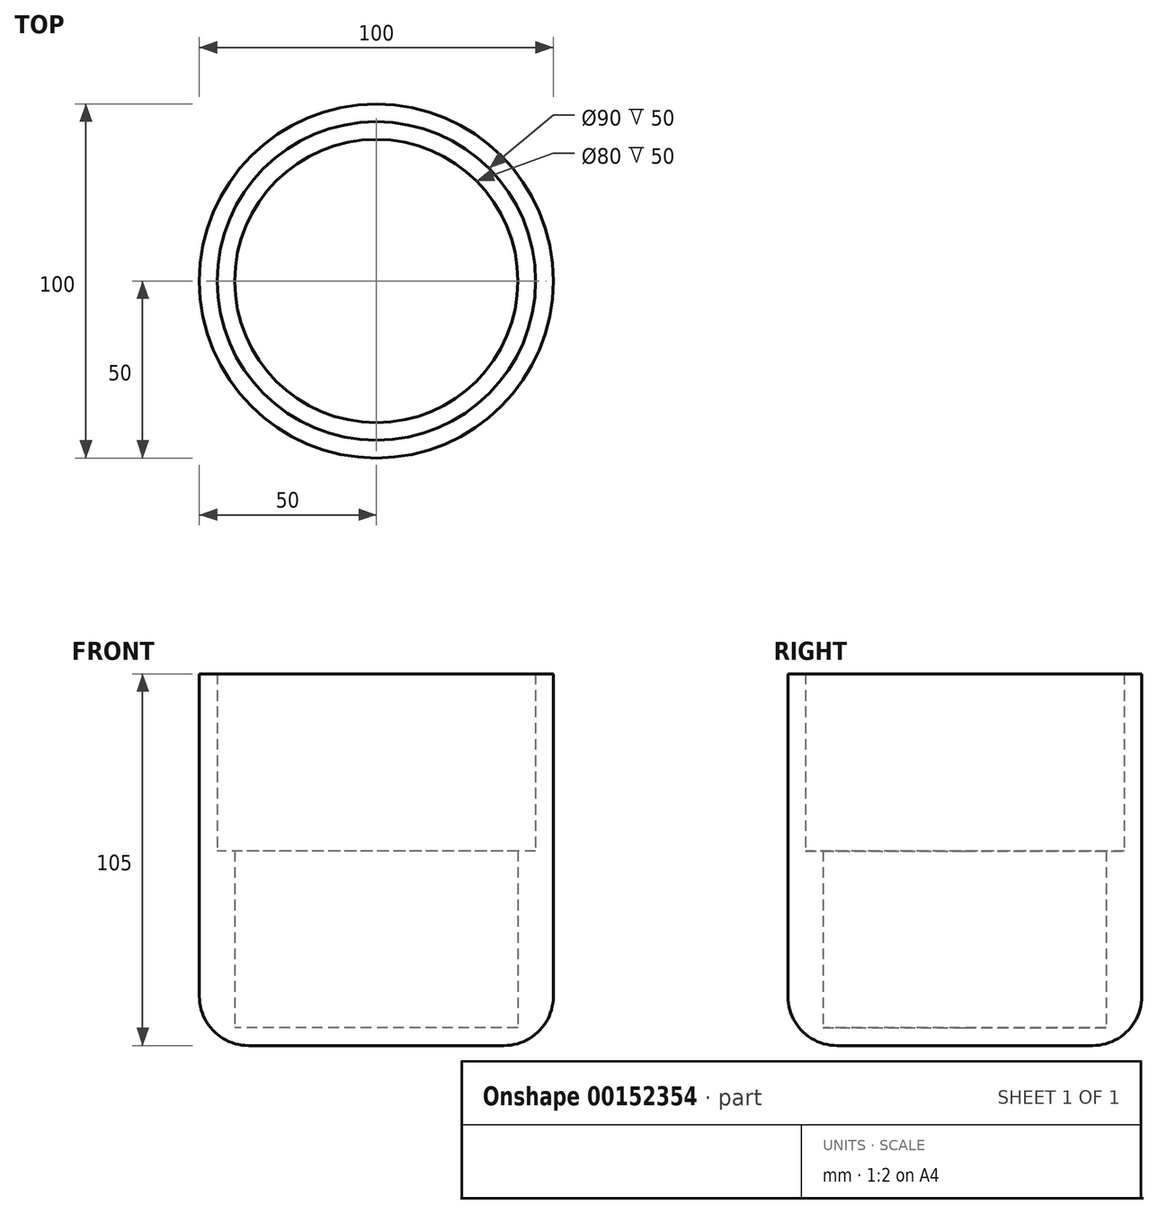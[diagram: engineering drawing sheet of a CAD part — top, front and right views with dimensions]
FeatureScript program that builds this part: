
annotation { "Feature Type Name" : "Feature", "Feature Type Description" : "" }
export const myFeature = defineFeature(function(context is Context, id is Id, definition is map)
    precondition{}
    {
        {
            var Q0;
            Q0=qCreatedBy(makeId("Top.planeOp"),FACE);
            var sketch = newSketch(context, id + "F0", { "sketchPlane" : qUnion([Q0])});
            skCircle(sketch, "E0", {"center": v(0, 0) * mm, "radius": 50 * mm});
            skCircle(sketch, "E1", {"center": v(0, 0) * mm, "radius": 45 * mm});
            skCircle(sketch, "E2", {"center": v(0, 0) * mm, "radius": 40 * mm});
            skSolve(sketch);
        }
        {
            var Q0;
            Q0=makeQuery(id+"F0.imprint","IMPRINT",FACE,{"disambiguationData":[TD([[makeQuery(id+"F0.imprint","IMPRINT",EDGE,{"derivedFrom":sQuery(id+"F0.wireOp",EDGE,"E0")}),1.0]])]});
            extrude(context, id + "F1", {"entities" : qUnion([Q0]), "depth" : 100 * mm});
        }
        {
            var Q0;
            Q0=makeQuery(id+"F0.imprint","IMPRINT",FACE,{"disambiguationData":[TD([[makeQuery(id+"F0.imprint","IMPRINT",EDGE,{"derivedFrom":sQuery(id+"F0.wireOp",EDGE,"E1")}),1.0]])]});
            var Q1;
            Q1=makeQuery(id+"F0.imprint","IMPRINT",FACE,{"disambiguationData":[TD([[makeQuery(id+"F0.imprint","IMPRINT",EDGE,{"derivedFrom":sQuery(id+"F0.wireOp",EDGE,"E0")}),1.0]])]});
            var Q2;
            Q2=makeQuery(id+"F0.imprint","IMPRINT",FACE,{"disambiguationData":[TD([[makeQuery(id+"F0.imprint","IMPRINT",EDGE,{"derivedFrom":sQuery(id+"F0.wireOp",EDGE,"E2")}),1.0]])]});
            extrude(context, id + "F2", {"entities" : qUnion([Q0, Q1, Q2]), "operationType" : NewBodyOperationType.ADD, "oppositeDirection" : true, "depth" : 5 * mm});
        }
        {
            var Q0;
            Q0=makeQuery(id+"F2.opExtrude","CAP_EDGE",EDGE,{"disambiguationData":[OSD([sQuery(id+"F0.wireOp",EDGE,"E0")])],"isStart":false});
            fillet(context, id + "F3", {"entities" : qUnion([Q0]), "radius" : 13.88 * mm, "tangentPropagation" : true, "allowEdgeOverflow" : false});
        }
        {
            var Q0;
            Q0=makeQuery(id+"F0.imprint","IMPRINT",FACE,{"disambiguationData":[TD([[makeQuery(id+"F0.imprint","IMPRINT",EDGE,{"derivedFrom":sQuery(id+"F0.wireOp",EDGE,"E1")}),1.0]])]});
            extrude(context, id + "F4", {"entities" : qUnion([Q0]), "operationType" : NewBodyOperationType.ADD, "depth" : 50 * mm});
        }
    });
